# Revit family: Duş için Geberit Duofix elemanı, 50 cm, duvar süzgeci ile, girişte 65–90 mm şap yüksekliği için_PRO_135685
name_source: partatom
category: Plumbing Fixtures
revit_build: Autodesk Revit 2018 (Build: 20190510_1515(x64)
units: mm (PartAtom-declared; Revit-internal decimal feet)

## family parameters
Always vertical = Yes
Cut with Voids When Loaded = No
OmniClass Number = 23.45.05.00
OmniClass Title = Sanitary Equipment
Part Type = Normal
Room Calculation Point = Yes
Round Connector Dimension = Use Diameter
Shared = No
Work Plane-Based = No

## types (1)
- 111.593.00.1 Duş için Geberit Duofix elemanı, 50 cm, duvar süzgeci ile, girişte 65–90 mm şap yüksekliği için
    Application purposes = Alçıpan yapılar için
Yarım veya oda yüksekliğinde Geberit Duofix sistem duvarlarına montaj için
Zemin seviyesindeki duşların drenajı için
Kompozit contalar için
Girişte ≥ 65 mm şap yükseklikleri için
    Application range = sanitary systems
    Article number key = 111.593.00.1
    BIM Content Version = GEB MG 1.5
    BIM Content revision date = 2021.12.01
    Brand = Geberit
    CW Connection = No
    Characteristics = EN 1253'ün gerekliliklerinden farklı olarak, sifon yüksekliği sadece 30 mm'dir.
Toz boya kaplı, kendinden destekli çerçeve
Dönebilir ayak plakaları
Ayak plakası derinliği, U profil UW 50 ve Geberit Duofix sistem rayları montajına uygundur
Sifon giriş yüksekliği ayarlanabilir
Kaplama kalınlığı 10–40 mm
Karo 2–26 mm karo yapıları için uygundur
Karo 2–35 mm karo yapıları için uygundur
Gerilimsiz sızdırmazlık bağlantısı için ayarlanabilir sızdırmazlık seviyesi
Yan atık su bağlantısı
Önceden monte edilmiş izolasyon bezi
Sızdırmazlık sistemleri bağlantısı için 10 cm çevreleyen izolasyon bezi
    Connection description 1 = sanitary out
    Connection diameter 1 = 40 mm  [stored 0.131234 ft]
    Connection type at connection 01 = DN40/ø40 Spigot
    D = 137 mm  [stored 0.449475 ft]
    Description = Duş için Geberit Duofix elemanı, 50 cm, duvar süzgeci ile, girişte 65–90 mm şap yüksekliği için
    Drenaj kapasitesi = 0.4 l/s
    EAN code basic data = 4025416289050
    GEB_culture = tr-TR
    GEB_generic_description = concealed support frame for shower
    GEB_generic_manufacturer = generic
    GEB_imperial_engineering = No
    GEB_metric_engineering = Yes
    GEB_pimversion = 22.02.12
    GEB_processing_type = T
    GEB_reference = PRO_135685
    GEB_translations = {"ATT_10673":"EAN code basic data","ATT_10753":"Drenaj kapasitesi","ATT_10864":"Sifon yüksekliği","applicationPurposes":"Application purposes","application_range":"Application range","brandName":"Brand","characteristics":"Characteristics","connection_description1":"Connection description 1","GEB_connection_diameter1":"Connection diameter 1","connection_type_c01":"Connection type at connection 01","content_creator":"BIM Content creator","content_date_changed":"BIM Content revision date","content_version":"BIM Content Version","key 1000":"Article number key","name":"Name","productBrand":"Product brand","scopeOfDelivery":"Scope of delivery","type":"Type","angle":"Angle","placement finished floor":"On Finished Floor Level","surface height":"Thickness of finished floor","warning":"Warning","fixed_material":"Main material","fixed_material_01":"Main material 01","fixed_material_02":"Main material 02","fixed_material_03":"Main material 03","fixed_material_04":"Main material 04"}
    GEB_use_DN = Yes
    H = 500 mm  [stored 1.64042 ft]
    H1 = -35 mm  [stored -0.114829 ft]
    HW Connection = No
    IfcDescription = Duş için Geberit Duofix elemanı, 50 cm, duvar süzgeci ile, girişte 65–90 mm şap yüksekliği için
    IfcExportAs = IfcSanitaryTerminal
    IfcExportType = USERDEFINED
    LOD300 = No
    LOD400 = Yes
    Main material = Geberit, Plastic, Opaque white
    Main material 01 = Geberit, Steel, Paint Finish, Blue
    Main material 02 = Geberit, Laminate, Ivory, Matte
    Main material 03 = Geberit, Steel, galvanized
    Main material 04 = Geberit, PE-HD, Black
    Manufacturer = Geberit
    Name = Duş için Geberit Duofix elemanı, 50 cm, duvar süzgeci ile, girişte 65–90 mm şap yüksekliği için
    Product brand = Duofix
    Scope of delivery = PE-HD bağlantı manşonu, ø 40 mm
Entegre giriş plakalı şablon kutusu kapağı
Sabitleme malzemesi
    Sifon yüksekliği = 30 mm
    Vent Connection = No
    W = 500 mm  [stored 1.64042 ft]
    Waste Connection = Yes
    cistern_front_offset = 21 mm
    cistern_width = 420 mm  [stored 1.37795 ft]
    frame_btm = 470 mm  [stored 1.54199 ft]
    h1 = 504 mm  [stored 1.65354 ft]
    outlet_flow = 0.0 L/s

note: [stored X ft] marks values corroborated as IEEE doubles in the binary element streams (Revit-internal decimal feet)

## geometry (parser evidence)
native form markers: Sweep x6
no freeform markers — native parametric forms only
